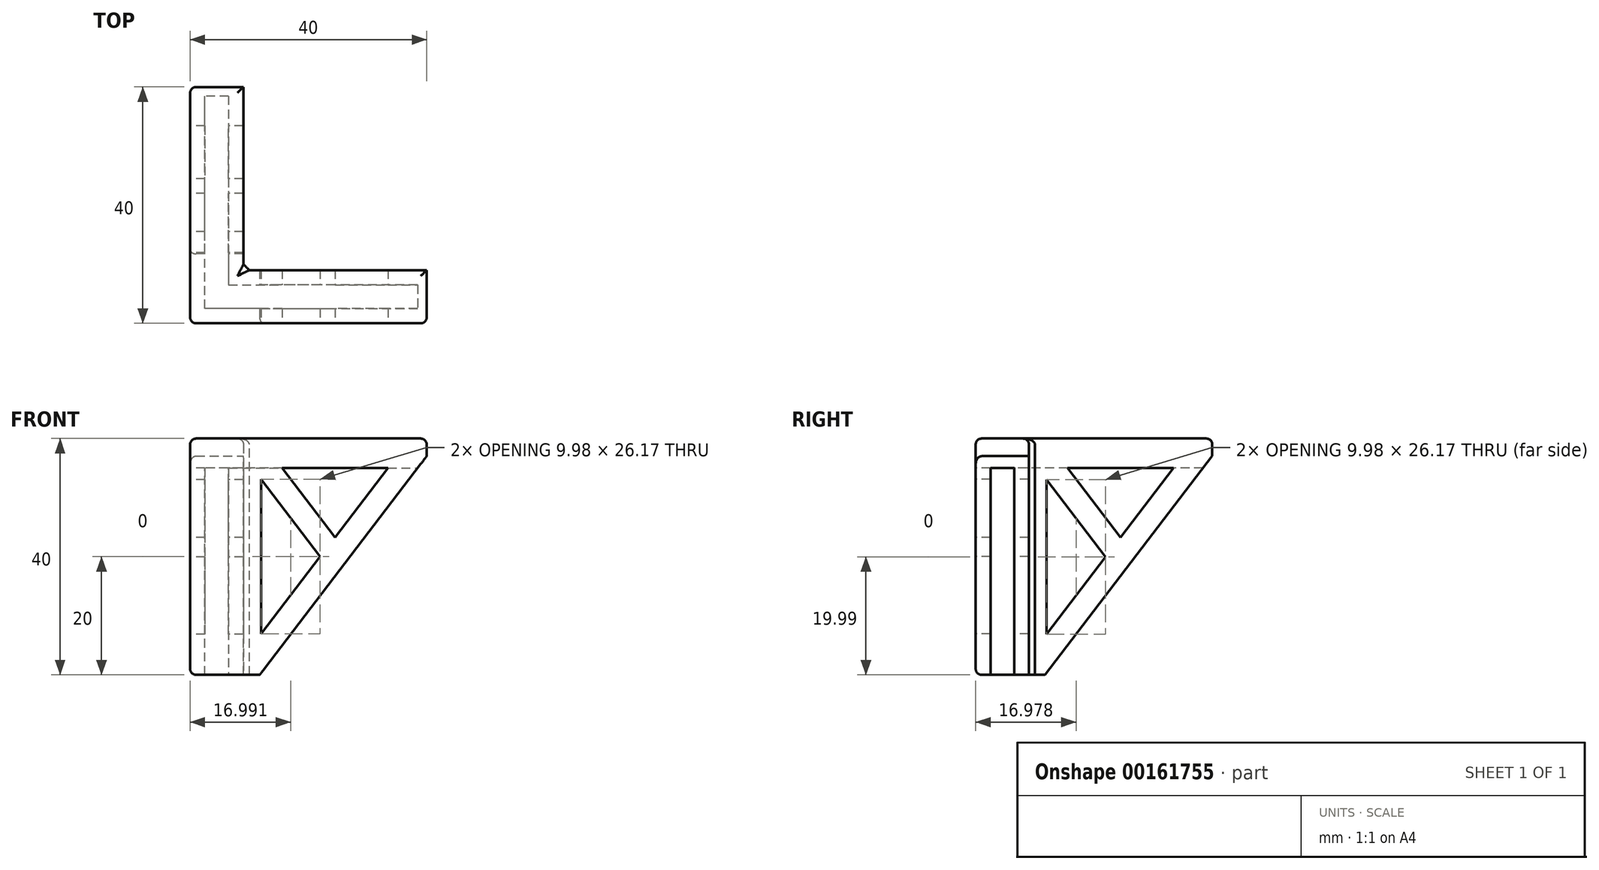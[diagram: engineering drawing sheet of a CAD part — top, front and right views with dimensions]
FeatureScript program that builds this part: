
annotation { "Feature Type Name" : "Feature", "Feature Type Description" : "" }
export const myFeature = defineFeature(function(context is Context, id is Id, definition is map)
    precondition{}
    {
        {
            var Q0;
            Q0=qCreatedBy(makeId("Top.planeOp"),FACE);
            var sketch = newSketch(context, id + "F0", { "sketchPlane" : qUnion([Q0])});
            skLineSegment(sketch, "E0.bottom", {"start": v(-0.94, -7.53) * mm, "end": v(39.06, -7.53) * mm});
            skLineSegment(sketch, "E0.top", {"start": v(-0.94, -47.53) * mm, "end": v(39.06, -47.53) * mm});
            skLineSegment(sketch, "E0.left", {"start": v(-0.94, -7.53) * mm, "end": v(-0.94, -47.53) * mm});
            skLineSegment(sketch, "E0.right", {"start": v(39.06, -7.53) * mm, "end": v(39.06, -47.53) * mm});
            skSolve(sketch);
        }
        {
            var Q0;
            Q0=makeQuery(id+"F0.imprint","IMPRINT",FACE,{"disambiguationData":[TD([[makeQuery(id+"F0.imprint","IMPRINT",EDGE,{"derivedFrom":sQuery(id+"F0.wireOp",EDGE,"E0.bottom")}),-1.0]])]});
            extrude(context, id + "F1", {"entities" : qUnion([Q0]), "depth" : 40 * mm});
        }
        {
            var Q0;
            Q0=makeQuery(id+"F1.opExtrude","CAP_FACE",FACE,{"disambiguationData":[OSD([sQuery(id+"F0.wireOp",EDGE,"E0.bottom"),sQuery(id+"F0.wireOp",EDGE,"E0.top"),sQuery(id+"F0.wireOp",EDGE,"E0.left"),sQuery(id+"F0.wireOp",EDGE,"E0.right")])],"isStart":true});
            var sketch = newSketch(context, id + "F2", { "sketchPlane" : qUnion([Q0])});
            skLineSegment(sketch, "E1", {"start": v(39.06, 45.03) * mm, "end": v(1.56, 45.03) * mm});
            skLineSegment(sketch, "E2", {"start": v(1.56, 45.03) * mm, "end": v(1.56, 7.53) * mm});
            skLineSegment(sketch, "E3", {"start": v(5.56, 7.53) * mm, "end": v(5.56, 41.03) * mm});
            skLineSegment(sketch, "E4", {"start": v(5.56, 41.03) * mm, "end": v(39.06, 41.03) * mm});
            skLineSegment(sketch, "E5", {"start": v(39.06, 38.53) * mm, "end": v(8.06, 38.53) * mm});
            skLineSegment(sketch, "E6", {"start": v(8.06, 38.53) * mm, "end": v(8.06, 7.53) * mm});
            skSolve(sketch);
        }
        {
            var Q0;
            {var subQ3=sQuery(id+"F2.wireOp",EDGE,"E1");Q0=makeQuery(id+"F2.imprint","IMPRINT",FACE,{"disambiguationData":[TD([[makeQuery(id+"F2.imprint","IMPRINT",EDGE,{"derivedFrom":subQ3}),1.0]])]});}
            extrude(context, id + "F3", {"entities" : qUnion([Q0]), "operationType" : NewBodyOperationType.REMOVE, "oppositeDirection" : true, "depth" : 35 * mm});
        }
        {
            var Q0;
            {var subQ0=sQuery(id+"F2.wireOp",EDGE,"E5");Q0=makeQuery(id+"F2.imprint","IMPRINT",FACE,{"disambiguationData":[TD([[makeQuery(id+"F2.imprint","IMPRINT",EDGE,{"derivedFrom":subQ0}),1.0]])]});}
            extrude(context, id + "F4", {"entities" : qUnion([Q0]), "operationType" : NewBodyOperationType.REMOVE, "endBound" : BoundingType.THROUGH_ALL, "oppositeDirection" : true, "depth" : 25 * mm});
        }
        {
            var Q0;
            Q0=makeQuery(id+"F4.boolean.opBoolean","COPY",EDGE,{"derivedFrom":makeQuery(id+"F4.opExtrude","SWEPT_EDGE",EDGE,{"disambiguationData":[OSD([sQuery(id+"F0.wireOp",EDGE,"E0.bottom"),sQuery(id+"F2.wireOp",EDGE,"E6")])]})});
            var Q1;
            Q1=makeQuery(id+"F1.opExtrude","SWEPT_EDGE",EDGE,{"disambiguationData":[OSD([sQuery(id+"F0.wireOp",EDGE,"E0.bottom"),sQuery(id+"F0.wireOp",EDGE,"E0.left")])]});
            var Q2;
            Q2=makeQuery(id+"F1.opExtrude","SWEPT_EDGE",EDGE,{"disambiguationData":[OSD([sQuery(id+"F0.wireOp",EDGE,"E0.top"),sQuery(id+"F0.wireOp",EDGE,"E0.left")])]});
            var Q3;
            Q3=makeQuery(id+"F4.boolean.opBoolean","COPY",EDGE,{"derivedFrom":makeQuery(id+"F4.opExtrude","SWEPT_EDGE",EDGE,{"disambiguationData":[OSD([sQuery(id+"F0.wireOp",EDGE,"E0.right"),sQuery(id+"F2.wireOp",EDGE,"E5")])]})});
            var Q4;
            Q4=makeQuery(id+"F1.opExtrude","SWEPT_EDGE",EDGE,{"disambiguationData":[OSD([sQuery(id+"F0.wireOp",EDGE,"E0.top"),sQuery(id+"F0.wireOp",EDGE,"E0.right")])]});
            var Q5;
            Q5=makeQuery(id+"F1.opExtrude","CAP_EDGE",EDGE,{"disambiguationData":[OSD([sQuery(id+"F0.wireOp",EDGE,"E0.right")])],"isStart":false});
            var Q6;
            Q6=makeQuery(id+"F1.opExtrude","CAP_EDGE",EDGE,{"disambiguationData":[OSD([sQuery(id+"F0.wireOp",EDGE,"E0.top")])],"isStart":false});
            var Q7;
            Q7=makeQuery(id+"F4.boolean.opBoolean","INTERSECT",EDGE,{"derivedFrom":[makeQuery(id+"F1.opExtrude","CAP_FACE",FACE,{"disambiguationData":[OSD([sQuery(id+"F0.wireOp",EDGE,"E0.bottom"),sQuery(id+"F0.wireOp",EDGE,"E0.top"),sQuery(id+"F0.wireOp",EDGE,"E0.left"),sQuery(id+"F0.wireOp",EDGE,"E0.right")])],"isStart":false}),makeQuery(id+"F4.opExtrude","SWEPT_FACE",FACE,{"disambiguationData":[OSD([sQuery(id+"F2.wireOp",EDGE,"E5")])]})]});
            var Q8;
            Q8=makeQuery(id+"F4.boolean.opBoolean","INTERSECT",EDGE,{"derivedFrom":[makeQuery(id+"F1.opExtrude","CAP_FACE",FACE,{"disambiguationData":[OSD([sQuery(id+"F0.wireOp",EDGE,"E0.bottom"),sQuery(id+"F0.wireOp",EDGE,"E0.top"),sQuery(id+"F0.wireOp",EDGE,"E0.left"),sQuery(id+"F0.wireOp",EDGE,"E0.right")])],"isStart":false}),makeQuery(id+"F4.opExtrude","SWEPT_FACE",FACE,{"disambiguationData":[OSD([sQuery(id+"F2.wireOp",EDGE,"E6")])]})]});
            var Q9;
            Q9=makeQuery(id+"F1.opExtrude","CAP_EDGE",EDGE,{"disambiguationData":[OSD([sQuery(id+"F0.wireOp",EDGE,"E0.bottom")])],"isStart":false});
            var Q10;
            Q10=makeQuery(id+"F1.opExtrude","CAP_EDGE",EDGE,{"disambiguationData":[OSD([sQuery(id+"F0.wireOp",EDGE,"E0.left")])],"isStart":false});
            var Q11;
            Q11=makeQuery(id+"F1.opExtrude","CAP_EDGE",EDGE,{"disambiguationData":[OSD([sQuery(id+"F0.wireOp",EDGE,"E0.top")])],"isStart":true});
            var Q12;
            Q12=makeQuery(id+"F4.boolean.opBoolean","COPY",EDGE,{"derivedFrom":makeQuery(id+"F4.opExtrude","CAP_EDGE",EDGE,{"disambiguationData":[OSD([sQuery(id+"F2.wireOp",EDGE,"E5")])],"isStart":true})});
            var Q13;
            Q13=makeQuery(id+"F4.boolean.opBoolean","COPY",EDGE,{"derivedFrom":makeQuery(id+"F4.opExtrude","CAP_EDGE",EDGE,{"disambiguationData":[OSD([sQuery(id+"F2.wireOp",EDGE,"E6")])],"isStart":true})});
            var Q14;
            Q14=makeQuery(id+"F1.opExtrude","CAP_EDGE",EDGE,{"disambiguationData":[OSD([sQuery(id+"F0.wireOp",EDGE,"E0.left")])],"isStart":true});
            var Q15;
            {var subQ0=sQuery(id+"F0.wireOp",EDGE,"E0.right");var subQ1=sQuery(id+"F0.wireOp",EDGE,"E0.top");Q15=makeQuery(id+"F3.boolean.opBoolean","SPLIT",EDGE,{"disambiguationData":[TD([makeQuery(id+"F1.opExtrude","SWEPT_FACE",FACE,{"disambiguationData":[OSD([subQ1])]})])],"derivedFrom":makeQuery(id+"F1.opExtrude","CAP_EDGE",EDGE,{"disambiguationData":[OSD([subQ0])],"isStart":true})});}
            var Q16;
            {var subQ0=sQuery(id+"F0.wireOp",EDGE,"E0.bottom");var subQ1=sQuery(id+"F0.wireOp",EDGE,"E0.right");Q16=makeQuery(id+"F3.boolean.opBoolean","SPLIT",EDGE,{"disambiguationData":[TD([makeQuery(id+"F1.opExtrude","SWEPT_FACE",FACE,{"disambiguationData":[OSD([subQ0])]})])],"derivedFrom":makeQuery(id+"F1.opExtrude","CAP_EDGE",EDGE,{"disambiguationData":[OSD([subQ1])],"isStart":true})});}
            var Q17;
            {var subQ0=sQuery(id+"F0.wireOp",EDGE,"E0.bottom");var subQ1=sQuery(id+"F0.wireOp",EDGE,"E0.right");Q17=makeQuery(id+"F3.boolean.opBoolean","SPLIT",EDGE,{"disambiguationData":[TD([makeQuery(id+"F1.opExtrude","SWEPT_FACE",FACE,{"disambiguationData":[OSD([subQ1])]})])],"derivedFrom":makeQuery(id+"F1.opExtrude","CAP_EDGE",EDGE,{"disambiguationData":[OSD([subQ0])],"isStart":true})});}
            var Q18;
            {var subQ0=sQuery(id+"F0.wireOp",EDGE,"E0.bottom");var subQ1=sQuery(id+"F0.wireOp",EDGE,"E0.left");Q18=makeQuery(id+"F3.boolean.opBoolean","SPLIT",EDGE,{"disambiguationData":[TD([makeQuery(id+"F1.opExtrude","SWEPT_FACE",FACE,{"disambiguationData":[OSD([subQ1])]})])],"derivedFrom":makeQuery(id+"F1.opExtrude","CAP_EDGE",EDGE,{"disambiguationData":[OSD([subQ0])],"isStart":true})});}
            fillet(context, id + "F5", {"entities" : qUnion([Q0, Q1, Q2, Q3, Q4, Q5, Q6, Q7, Q8, Q9, Q10, Q11, Q12, Q13, Q14, Q15, Q16, Q17, Q18]), "radius" : 1 * mm, "tangentPropagation" : true, "allowEdgeOverflow" : false});
        }
        {
            var Q0;
            Q0=makeQuery(id+"F4.boolean.opBoolean","COPY",EDGE,{"derivedFrom":makeQuery(id+"F4.opExtrude","SWEPT_EDGE",EDGE,{"disambiguationData":[OSD([sQuery(id+"F2.wireOp",EDGE,"E5"),sQuery(id+"F2.wireOp",EDGE,"E6")])]})});
            chamfer(context, id + "F6", {"entities" : qUnion([Q0]), "width" : 1 * mm, "tangentPropagation" : true});
        }
        {
            var Q0;
            Q0=makeQuery(id+"F1.opExtrude","SWEPT_FACE",FACE,{"disambiguationData":[OSD([sQuery(id+"F0.wireOp",EDGE,"E0.top")])]});
            var sketch = newSketch(context, id + "F7", { "sketchPlane" : qUnion([Q0])});
            skLineSegment(sketch, "E7", {"start": v(9.06, 39) * mm, "end": v(9.06, 1) * mm});
            skLineSegment(sketch, "E8", {"start": v(11.57, 39) * mm, "end": v(38.06, 4.3) * mm});
            skLineSegment(sketch, "E9", {"start": v(9.06, 35.7) * mm, "end": v(35.54, 1) * mm});
            skLineSegment(sketch, "E10", {"start": v(35.54, 39) * mm, "end": v(9.06, 4.3) * mm});
            skLineSegment(sketch, "E11", {"start": v(11.57, 1) * mm, "end": v(38.06, 35.7) * mm});
            skLineSegment(sketch, "E12", {"start": v(14.63, 35) * mm, "end": v(32.5, 35) * mm});
            skLineSegment(sketch, "E13", {"start": v(11.06, 33.08) * mm, "end": v(11.06, 6.92) * mm});
            skLineSegment(sketch, "E14", {"start": v(38.06, 35.7) * mm, "end": v(39.14, 37.12) * mm});
            skLineSegment(sketch, "E15", {"start": v(11.57, 1) * mm, "end": v(10.81, 0) * mm});
            skLineSegment(sketch, "E16", {"start": v(10.81, 0) * mm, "end": v(39.07, 0) * mm});
            skLineSegment(sketch, "E17", {"start": v(39.07, 0) * mm, "end": v(39.14, 37.12) * mm});
            skSolve(sketch);
        }
        {
            var Q0;
            {var subQ0=sQuery(id+"F7.wireOp",EDGE,"E12");Q0=makeQuery(id+"F7.imprint","IMPRINT",FACE,{"disambiguationData":[TD([[makeQuery(id+"F7.imprint","IMPRINT",EDGE,{"derivedFrom":subQ0}),-1.0]])]});}
            var Q1;
            {var subQ0=sQuery(id+"F7.wireOp",EDGE,"E13");Q1=makeQuery(id+"F7.imprint","IMPRINT",FACE,{"disambiguationData":[TD([[makeQuery(id+"F7.imprint","IMPRINT",EDGE,{"derivedFrom":subQ0}),1.0]])]});}
            var Q2;
            {var subQ0=sQuery(id+"F7.wireOp",EDGE,"tIHaNC7f-m8fM-WyO5-XY3W-4vOh1iQVT0BU");Q2=makeQuery(id+"F7.imprint","IMPRINT",FACE,{"disambiguationData":[TD([[makeQuery(id+"F7.imprint","IMPRINT",EDGE,{"derivedFrom":subQ0}),1.0]])]});}
            var Q3;
            {var subQ0=sQuery(id+"F7.wireOp",EDGE,"aRXLlso4-VBMh-aw2C-FCt8-SyfEA6FeEp6y");Q3=makeQuery(id+"F7.imprint","IMPRINT",FACE,{"disambiguationData":[TD([[makeQuery(id+"F7.imprint","IMPRINT",EDGE,{"derivedFrom":subQ0}),-1.0]])]});}
            extrude(context, id + "F8", {"entities" : qUnion([Q0, Q1, Q2, Q3]), "operationType" : NewBodyOperationType.REMOVE, "endBound" : BoundingType.THROUGH_ALL, "oppositeDirection" : true, "depth" : 25 * mm});
        }
        {
            var Q0;
            Q0=makeQuery(id+"F1.opExtrude","SWEPT_FACE",FACE,{"disambiguationData":[OSD([sQuery(id+"F0.wireOp",EDGE,"E0.left")])]});
            var sketch = newSketch(context, id + "F9", { "sketchPlane" : qUnion([Q0])});
            skLineSegment(sketch, "E18", {"start": v(37.54, 39) * mm, "end": v(37.54, 1) * mm});
            skLineSegment(sketch, "E19.MirrorCS", {"start": v(35.54, 33.07) * mm, "end": v(35.54, 6.9) * mm});
            skLineSegment(sketch, "E20.MirrorCS", {"start": v(37.54, 35.7) * mm, "end": v(11.06, 1) * mm});
            skLineSegment(sketch, "E21.MirrorCS", {"start": v(35.03, 39) * mm, "end": v(8.54, 4.29) * mm});
            skLineSegment(sketch, "E22.MirrorCS", {"start": v(31.98, 35) * mm, "end": v(14.1, 35) * mm});
            skLineSegment(sketch, "E23.MirrorCS", {"start": v(11.06, 39) * mm, "end": v(37.54, 4.29) * mm});
            skLineSegment(sketch, "E24.MirrorCS", {"start": v(35.03, 1) * mm, "end": v(8.54, 35.7) * mm});
            skLineSegment(sketch, "E25", {"start": v(35.03, 1) * mm, "end": v(35.78, 0) * mm});
            skLineSegment(sketch, "E26", {"start": v(8.54, 35.7) * mm, "end": v(7.43, 37.15) * mm});
            skLineSegment(sketch, "E27", {"start": v(7.43, 37.15) * mm, "end": v(7.43, 0) * mm});
            skLineSegment(sketch, "E28", {"start": v(7.43, 0) * mm, "end": v(35.78, 0) * mm});
            skSolve(sketch);
        }
        {
            var Q0;
            {var subQ0=sQuery(id+"F9.wireOp",EDGE,"E22.MirrorCS");Q0=makeQuery(id+"F9.imprint","IMPRINT",FACE,{"disambiguationData":[TD([[makeQuery(id+"F9.imprint","IMPRINT",EDGE,{"derivedFrom":subQ0}),1.0]])]});}
            var Q1;
            {var subQ0=sQuery(id+"F9.wireOp",EDGE,"6f1311b4-482e-4614-a43a-64ca706b4e5f0.MirrorCS");Q1=makeQuery(id+"F9.imprint","IMPRINT",FACE,{"disambiguationData":[TD([[makeQuery(id+"F9.imprint","IMPRINT",EDGE,{"derivedFrom":subQ0}),1.0]])]});}
            var Q2;
            {var subQ0=sQuery(id+"F9.wireOp",EDGE,"9c941e44-beb6-430b-abd9-2cc7d5a94ad80.MirrorCS");Q2=makeQuery(id+"F9.imprint","IMPRINT",FACE,{"disambiguationData":[TD([[makeQuery(id+"F9.imprint","IMPRINT",EDGE,{"derivedFrom":subQ0}),-1.0]])]});}
            var Q3;
            {var subQ0=sQuery(id+"F9.wireOp",EDGE,"E19.MirrorCS");Q3=makeQuery(id+"F9.imprint","IMPRINT",FACE,{"disambiguationData":[TD([[makeQuery(id+"F9.imprint","IMPRINT",EDGE,{"derivedFrom":subQ0}),-1.0]])]});}
            extrude(context, id + "F10", {"entities" : qUnion([Q0, Q1, Q2, Q3]), "operationType" : NewBodyOperationType.REMOVE, "endBound" : BoundingType.THROUGH_ALL, "oppositeDirection" : true, "depth" : 25 * mm});
        }
        {
            var Q0;
            {var subQ0=sQuery(id+"F7.wireOp",EDGE,"E11");var subQ1=sQuery(id+"F7.wireOp",EDGE,"E8");var subQ2=makeQuery(id+"F7.imprint","INTERSECT",VERTEX,{"derivedFrom":[subQ1,subQ0]});Q0=makeQuery(id+"F7.imprint","IMPRINT",FACE,{"disambiguationData":[TD([[makeQuery(id+"F7.imprint","IMPRINT",EDGE,{"disambiguationData":[TD([[subQ2,1.0]])],"derivedFrom":subQ0}),-1.0]])]});}
            var Q1;
            {var subQ0=sQuery(id+"F7.wireOp",EDGE,"E8");var subQ4=sQuery(id+"F7.wireOp",EDGE,"E11");var subQ5=makeQuery(id+"F7.imprint","INTERSECT",VERTEX,{"derivedFrom":[subQ0,subQ4]});Q1=makeQuery(id+"F7.imprint","IMPRINT",FACE,{"disambiguationData":[TD([[makeQuery(id+"F7.imprint","IMPRINT",EDGE,{"disambiguationData":[TD([[subQ5,-1.0]])],"derivedFrom":subQ0}),1.0]])]});}
            var Q2;
            {var subQ0=sQuery(id+"F7.wireOp",EDGE,"E9");var subQ4=sQuery(id+"F7.wireOp",EDGE,"E11");var subQ5=makeQuery(id+"F7.imprint","INTERSECT",VERTEX,{"derivedFrom":[subQ0,subQ4]});Q2=makeQuery(id+"F7.imprint","IMPRINT",FACE,{"disambiguationData":[TD([[makeQuery(id+"F7.imprint","IMPRINT",EDGE,{"disambiguationData":[TD([[subQ5,-1.0]])],"derivedFrom":subQ0}),-1.0]])]});}
            extrude(context, id + "F11", {"entities" : qUnion([Q0, Q1, Q2]), "operationType" : NewBodyOperationType.REMOVE, "endBound" : BoundingType.THROUGH_ALL, "oppositeDirection" : true, "depth" : 25 * mm});
        }
        {
            var Q0;
            {var subQ1=sQuery(id+"F9.wireOp",EDGE,"E24.MirrorCS");var subQ7=makeQuery(id+"F9.imprint","INTERSECT",VERTEX,{"derivedFrom":[sQuery(id+"F9.wireOp",EDGE,"E21.MirrorCS"),subQ1]});Q0=makeQuery(id+"F9.imprint","IMPRINT",FACE,{"disambiguationData":[TD([[makeQuery(id+"F9.imprint","IMPRINT",EDGE,{"disambiguationData":[TD([[subQ7,1.0]])],"derivedFrom":subQ1}),1.0]])]});}
            var Q1;
            {var subQ0=sQuery(id+"F9.wireOp",EDGE,"E24.MirrorCS");var subQ1=sQuery(id+"F9.wireOp",EDGE,"E20.MirrorCS");var subQ2=makeQuery(id+"F9.imprint","INTERSECT",VERTEX,{"derivedFrom":[subQ1,subQ0]});Q1=makeQuery(id+"F9.imprint","IMPRINT",FACE,{"disambiguationData":[TD([[makeQuery(id+"F9.imprint","IMPRINT",EDGE,{"disambiguationData":[TD([[subQ2,-1.0]])],"derivedFrom":subQ1}),1.0]])]});}
            var Q2;
            {var subQ8=sQuery(id+"F9.wireOp",EDGE,"E25");Q2=makeQuery(id+"F9.imprint","IMPRINT",FACE,{"disambiguationData":[TD([[makeQuery(id+"F9.imprint","IMPRINT",EDGE,{"derivedFrom":subQ8}),-1.0]])]});}
            var Q3;
            Q3=sQuery(id+"F9.wireOp",EDGE,"E27");
            var Q4;
            Q4=sQuery(id+"F9.wireOp",EDGE,"E26");
            var Q5;
            Q5=sQuery(id+"F9.wireOp",EDGE,"E24.MirrorCS");
            var Q6;
            Q6=sQuery(id+"F9.wireOp",EDGE,"E25");
            var Q7;
            Q7=sQuery(id+"F9.wireOp",EDGE,"E28");
            extrude(context, id + "F12", {"entities" : qUnion([Q0, Q1, Q2]), "operationType" : NewBodyOperationType.REMOVE, "surfaceEntities" : qUnion([Q3, Q4, Q5, Q6, Q7]), "endBound" : BoundingType.THROUGH_ALL, "oppositeDirection" : true, "depth" : 25 * mm});
        }
        {
            var Q0;
            {var subQ6=sQuery(id+"F7.wireOp",EDGE,"E14");Q0=makeQuery(id+"F7.imprint","IMPRINT",FACE,{"disambiguationData":[TD([[makeQuery(id+"F7.imprint","IMPRINT",EDGE,{"derivedFrom":subQ6}),-1.0]])]});}
            extrude(context, id + "F13", {"entities" : qUnion([Q0]), "operationType" : NewBodyOperationType.REMOVE, "endBound" : BoundingType.THROUGH_ALL, "oppositeDirection" : true, "depth" : 25 * mm});
        }
    });
